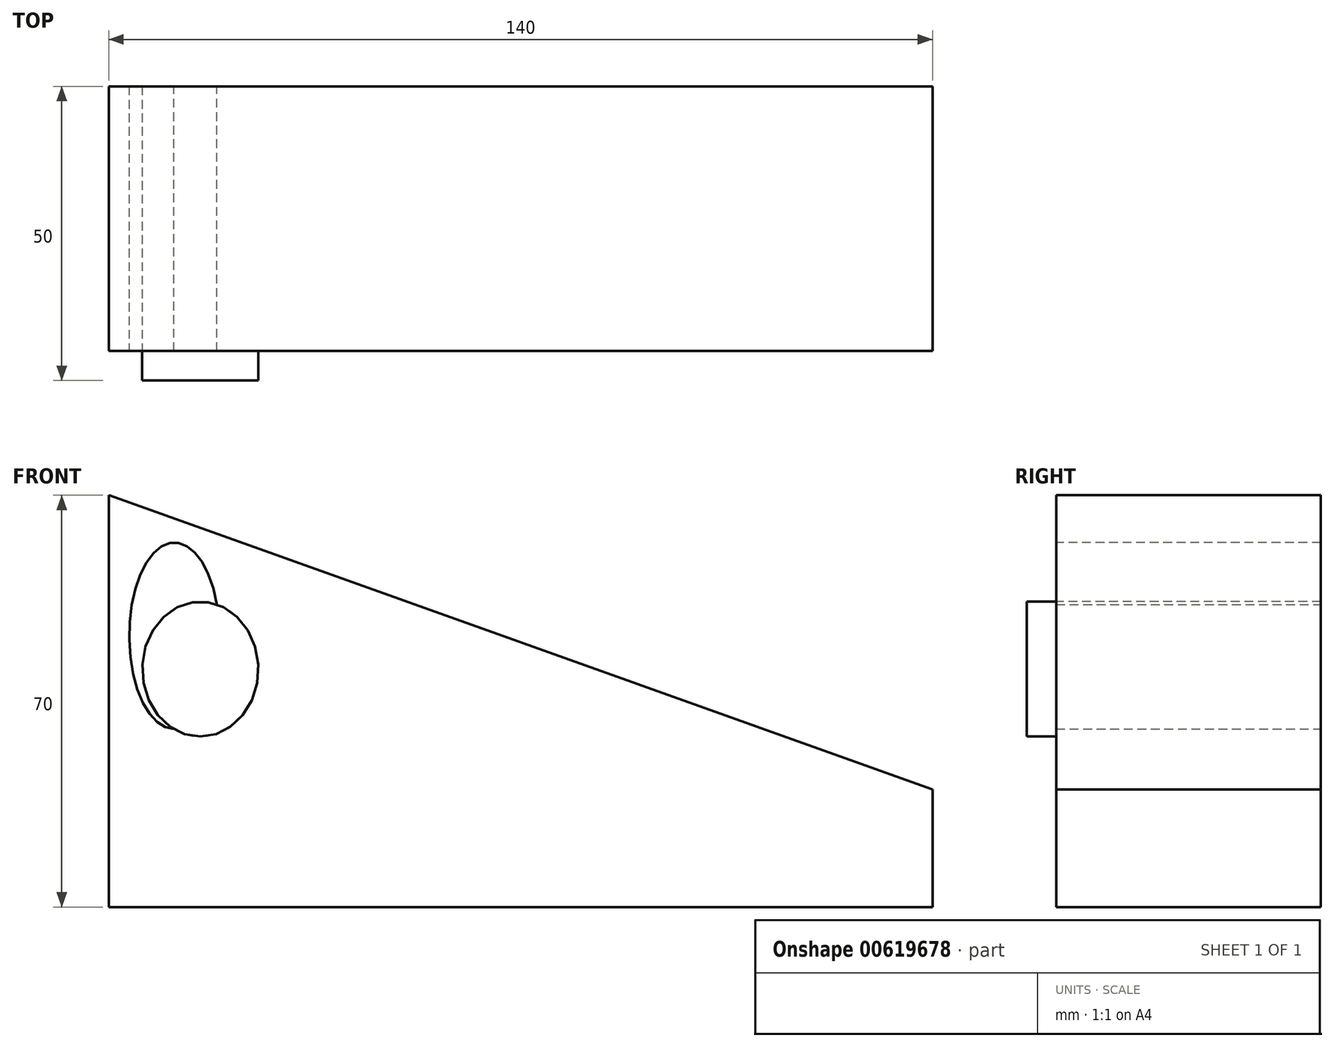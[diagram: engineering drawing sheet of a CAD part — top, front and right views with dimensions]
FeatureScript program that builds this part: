
annotation { "Feature Type Name" : "Feature", "Feature Type Description" : "" }
export const myFeature = defineFeature(function(context is Context, id is Id, definition is map)
    precondition{}
    {
        {
            var Q0;
            Q0=qCreatedBy(makeId("Front.planeOp"),FACE);
            var sketch = newSketch(context, id + "F0", { "sketchPlane" : qUnion([Q0])});
            skLineSegment(sketch, "E0", {"start": v(0, 0) * mm, "end": v(140, 0) * mm});
            skLineSegment(sketch, "E1", {"start": v(140, 0) * mm, "end": v(140, 20) * mm});
            skLineSegment(sketch, "E2", {"start": v(140, 20) * mm, "end": v(140, 0) * mm});
            skLineSegment(sketch, "E3", {"start": v(0, 0) * mm, "end": v(0, 70) * mm});
            skLineSegment(sketch, "E4", {"start": v(0, 70) * mm, "end": v(140, 20) * mm});
            skEllipse(sketch, "E5", {"center": v(11.13, 46.1) * mm, "majorRadius": 15.86 * mm, "minorRadius": 7.68 * mm, "majorAxis": v(0, -1)});
            skSolve(sketch);
        }
        {
            var Q0;
            Q0=makeQuery(id+"F0.imprint","IMPRINT",FACE,{"disambiguationData":[TD([[makeQuery(id+"F0.imprint","IMPRINT",EDGE,{"derivedFrom":sQuery(id+"F0.wireOp",EDGE,"E0")}),1.0]])]});
            extrude(context, id + "F1", {"entities" : qUnion([Q0]), "depth" : 20 * mm, "offsetDistance" : 25 * mm});
        }
        {
            var Q0;
            Q0=qCreatedBy(makeId("Front.planeOp"),FACE);
            var sketch = newSketch(context, id + "F2", { "sketchPlane" : qUnion([Q0])});
            skEllipse(sketch, "E6", {"center": v(15.54, 40.44) * mm, "majorRadius": 11.47 * mm, "minorRadius": 9.86 * mm, "majorAxis": v(0, -1)});
            skSolve(sketch);
        }
        {
            var Q0;
            Q0=makeQuery(id+"F2.imprint","IMPRINT",FACE,{"disambiguationData":[TD([[makeQuery(id+"F2.imprint","IMPRINT",EDGE,{"derivedFrom":sQuery(id+"F2.wireOp",EDGE,"E6")}),1.0]])]});
            extrude(context, id + "F3", {"entities" : qUnion([Q0]), "operationType" : NewBodyOperationType.ADD, "depth" : 25 * mm, "offsetDistance" : 25 * mm});
        }
        {
            var Q0;
            Q0=makeQuery(id+"F3.opExtrude","CAP_FACE",FACE,{"disambiguationData":[OSD([sQuery(id+"F2.wireOp",EDGE,"E6")])],"isStart":false});
            extrude(context, id + "F4", {"entities" : qUnion([Q0]), "operationType" : NewBodyOperationType.ADD, "oppositeDirection" : true, "depth" : 10 * mm, "offsetDistance" : 25 * mm});
        }
        {
            var Q0;
            Q0=makeQuery(id+"F3.boolean.opBoolean","MERGE",FACE,{"derivedFrom":[makeQuery(id+"F1.opExtrude","CAP_FACE",FACE,{"disambiguationData":[OSD([sQuery(id+"F0.wireOp",EDGE,"E0"),sQuery(id+"F0.wireOp",EDGE,"E2"),sQuery(id+"F0.wireOp",EDGE,"E3"),sQuery(id+"F0.wireOp",EDGE,"E4"),sQuery(id+"F0.wireOp",EDGE,"E5")])],"isStart":true}),makeQuery(id+"F3.opExtrude","CAP_FACE",FACE,{"disambiguationData":[OSD([sQuery(id+"F2.wireOp",EDGE,"E6")])],"isStart":true})]});
            extrude(context, id + "F5", {"entities" : qUnion([Q0]), "operationType" : NewBodyOperationType.ADD, "depth" : 25 * mm, "offsetDistance" : 25 * mm});
        }
    });
